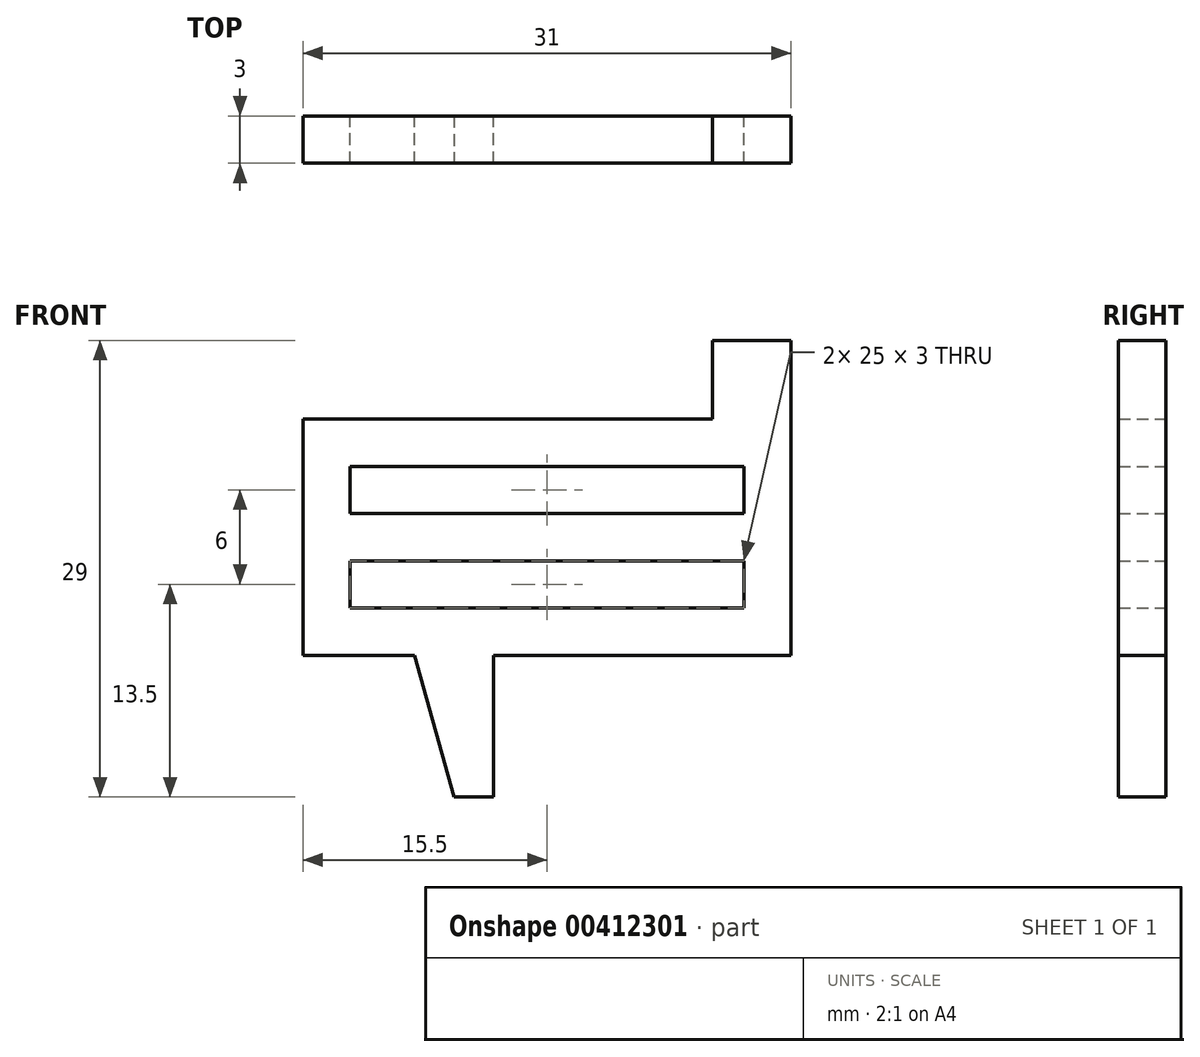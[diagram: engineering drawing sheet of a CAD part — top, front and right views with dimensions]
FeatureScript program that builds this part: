
annotation { "Feature Type Name" : "Feature", "Feature Type Description" : "" }
export const myFeature = defineFeature(function(context is Context, id is Id, definition is map)
    precondition{}
    {
        {
            var Q0;
            Q0=qCreatedBy(makeId("Front.planeOp"),FACE);
            var sketch = newSketch(context, id + "F0", { "sketchPlane" : qUnion([Q0])});
            skLineSegment(sketch, "E0.bottom", {"start": v(15.5, 7.5) * mm, "end": v(-15.5, 7.5) * mm});
            skLineSegment(sketch, "E0.top", {"start": v(15.5, -7.5) * mm, "end": v(-15.5, -7.5) * mm});
            skLineSegment(sketch, "E0.left", {"start": v(15.5, 7.5) * mm, "end": v(15.5, -7.5) * mm});
            skLineSegment(sketch, "E0.right", {"start": v(-15.5, 7.5) * mm, "end": v(-15.5, -7.5) * mm});
            skPoint(sketch, "E0.middle", {"position": v(0, 0) * mm});
            skLineSegment(sketch, "E1.bottom", {"start": v(12.5, 4.5) * mm, "end": v(-12.5, 4.5) * mm});
            skLineSegment(sketch, "E1.top", {"start": v(12.5, 1.5) * mm, "end": v(-12.5, 1.5) * mm});
            skLineSegment(sketch, "E1.left", {"start": v(12.5, 4.5) * mm, "end": v(12.5, 1.5) * mm});
            skLineSegment(sketch, "E1.right", {"start": v(-12.5, 4.5) * mm, "end": v(-12.5, 1.5) * mm});
            skPoint(sketch, "E1.middle", {"position": v(0, 3) * mm});
            skLineSegment(sketch, "E2.bottom", {"start": v(12.5, -1.5) * mm, "end": v(-12.5, -1.5) * mm});
            skLineSegment(sketch, "E2.top", {"start": v(12.5, -4.5) * mm, "end": v(-12.5, -4.5) * mm});
            skLineSegment(sketch, "E2.left", {"start": v(12.5, -1.5) * mm, "end": v(12.5, -4.5) * mm});
            skLineSegment(sketch, "E2.right", {"start": v(-12.5, -1.5) * mm, "end": v(-12.5, -4.5) * mm});
            skPoint(sketch, "E2.middle", {"position": v(0, -3) * mm});
            skLineSegment(sketch, "E3.bottom", {"start": v(15.5, 7.5) * mm, "end": v(10.5, 7.5) * mm});
            skLineSegment(sketch, "E3.top", {"start": v(15.5, 12.5) * mm, "end": v(10.5, 12.5) * mm});
            skLineSegment(sketch, "E3.left", {"start": v(15.5, 7.5) * mm, "end": v(15.5, 12.5) * mm});
            skLineSegment(sketch, "E3.right", {"start": v(10.5, 7.5) * mm, "end": v(10.5, 12.5) * mm});
            skLineSegment(sketch, "E4.bottom", {"start": v(-3.41, -7.5) * mm, "end": v(-8.41, -7.5) * mm});
            skLineSegment(sketch, "E4.top", {"start": v(-3.41, -16.5) * mm, "end": v(-8.41, -16.5) * mm});
            skLineSegment(sketch, "E4.left", {"start": v(-3.41, -7.5) * mm, "end": v(-3.41, -16.5) * mm});
            skLineSegment(sketch, "E4.right", {"start": v(-8.41, -7.5) * mm, "end": v(-8.41, -16.5) * mm});
            skSolve(sketch);
        }
        {
            var Q0;
            Q0 = qSketchRegion(id + "F0", true);
            extrude(context, id + "F1", {"entities" : qUnion([Q0]), "depth" : 3 * mm});
        }
        {
            var Q0;
            Q0=makeQuery(id+"F1.opExtrude","CAP_FACE",FACE,{"disambiguationData":[OSD([sQuery(id+"F0.wireOp",EDGE,"E0.bottom"),sQuery(id+"F0.wireOp",EDGE,"E0.top"),sQuery(id+"F0.wireOp",EDGE,"E0.left"),sQuery(id+"F0.wireOp",EDGE,"E0.right"),sQuery(id+"F0.wireOp",EDGE,"E1.bottom"),sQuery(id+"F0.wireOp",EDGE,"E1.top"),sQuery(id+"F0.wireOp",EDGE,"E1.left"),sQuery(id+"F0.wireOp",EDGE,"E1.right"),sQuery(id+"F0.wireOp",EDGE,"E2.bottom"),sQuery(id+"F0.wireOp",EDGE,"E2.top"),sQuery(id+"F0.wireOp",EDGE,"E2.left"),sQuery(id+"F0.wireOp",EDGE,"E2.right"),sQuery(id+"F0.wireOp",EDGE,"E3.top"),sQuery(id+"F0.wireOp",EDGE,"E3.left"),sQuery(id+"F0.wireOp",EDGE,"E3.right"),sQuery(id+"F0.wireOp",EDGE,"E4.top"),sQuery(id+"F0.wireOp",EDGE,"E4.left"),sQuery(id+"F0.wireOp",EDGE,"E4.right")])],"isStart":false});
            var sketch = newSketch(context, id + "F2", { "sketchPlane" : qUnion([Q0])});
            skLineSegment(sketch, "E5", {"start": v(-8.41, -7.5) * mm, "end": v(-5.91, -16.5) * mm});
            skLineSegment(sketch, "E6", {"start": v(-5.91, -16.5) * mm, "end": v(-8.41, -16.5) * mm});
            skLineSegment(sketch, "E7", {"start": v(-8.41, -16.5) * mm, "end": v(-8.41, -7.5) * mm});
            skSolve(sketch);
        }
        {
            var Q0;
            Q0 = qSketchRegion(id + "F2", true);
            extrude(context, id + "F3", {"entities" : qUnion([Q0]), "operationType" : NewBodyOperationType.REMOVE, "oppositeDirection" : true, "depth" : 25 * mm});
        }
    });
